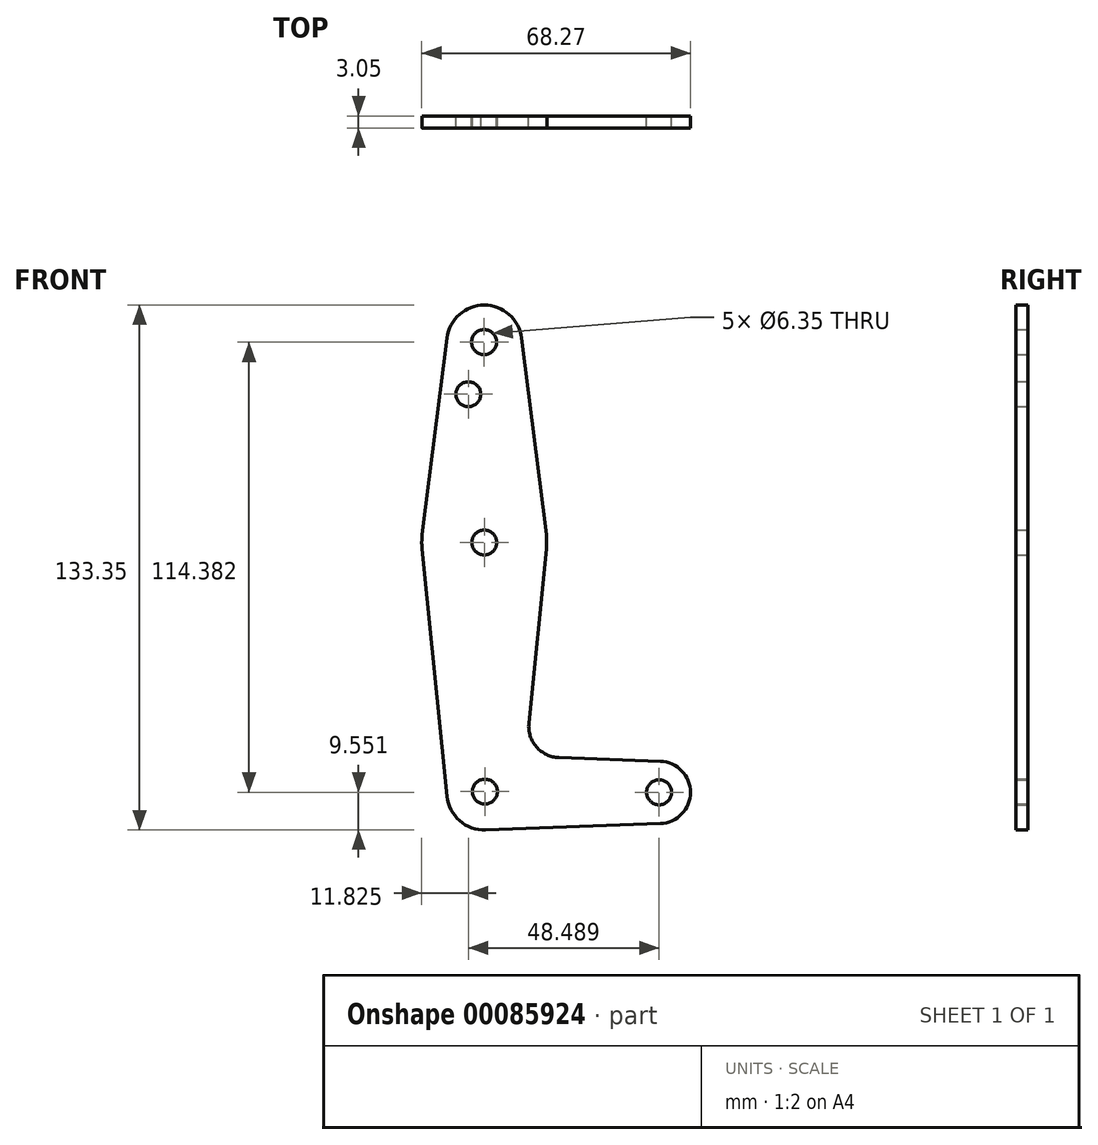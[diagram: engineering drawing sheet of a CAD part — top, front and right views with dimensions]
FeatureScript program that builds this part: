
annotation { "Feature Type Name" : "Feature", "Feature Type Description" : "" }
export const myFeature = defineFeature(function(context is Context, id is Id, definition is map)
    precondition{}
    {
        {
            var Q0;
            Q0=qCreatedBy(makeId("Front.planeOp"),FACE);
            var sketch = newSketch(context, id + "F0", { "sketchPlane" : qUnion([Q0])});
            skLineSegment(sketch, "E0", {"start": v(0, 114.3) * mm, "end": v(0, 0) * mm, "construction": true});
            skLineSegment(sketch, "E1", {"start": v(0, 0) * mm, "end": v(44.45, 0) * mm, "construction": true});
            skCircle(sketch, "E2", {"center": v(0, 0) * mm, "radius": 9.53 * mm});
            skCircle(sketch, "E3", {"center": v(0, 63.5) * mm, "radius": 15.88 * mm});
            skCircle(sketch, "E4", {"center": v(0, 114.3) * mm, "radius": 9.53 * mm});
            skCircle(sketch, "E5", {"center": v(44.45, 0) * mm, "radius": 7.94 * mm});
            skLineSegment(sketch, "E6", {"start": v(-9.45, 115.5) * mm, "end": v(-15.75, 65.48) * mm});
            skCircle(sketch, "E7", {"center": v(-0.05, 114.41) * mm, "radius": 3.18 * mm});
            skCircle(sketch, "E8", {"center": v(0, 63.5) * mm, "radius": 3.18 * mm});
            skCircle(sketch, "E9", {"center": v(0.16, 0.2) * mm, "radius": 3.18 * mm});
            skCircle(sketch, "E10", {"center": v(44.43, 0.03) * mm, "radius": 3.18 * mm});
            skCircle(sketch, "E11", {"center": v(-4.05, 101.17) * mm, "radius": 3.18 * mm});
            skLineSegment(sketch, "E12", {"start": v(15.75, 65.48) * mm, "end": v(9.45, 115.5) * mm});
            skLineSegment(sketch, "E13", {"start": v(15.8, 61.91) * mm, "end": v(11.34, 17.6) * mm});
            skLineSegment(sketch, "E14", {"start": v(0.34, -9.52) * mm, "end": v(44.73, -7.93) * mm});
            skLineSegment(sketch, "E15", {"start": v(18.97, 8.85) * mm, "end": v(44.73, 7.93) * mm});
            skLineSegment(sketch, "E16", {"start": v(-15.8, 61.91) * mm, "end": v(-9.48, -0.95) * mm});
            skArc(sketch, "E17.filletArc", {"start": v(11.34, 17.6) * mm, "mid": v(13.26, 11.57) * mm, "end": v(18.97, 8.85) * mm});
            skText(sketch, "E18", { "text": "The volume of the object is 0.702 in3.", "fontName": "OpenSans-Regular.ttf"});
            const initialGuessF0  = {"E18": [-0.11229, -0.05677, 1, 0, 0.02676]};
            skSetInitialGuess(sketch, initialGuessF0);
            skSolve(sketch);
        }
        {
            var Q0;
            {var subQ0=sQuery(id+"F0.wireOp",EDGE,"E6");Q0=makeQuery(id+"F0.imprint","IMPRINT",FACE,{"disambiguationData":[TD([[makeQuery(id+"F0.imprint","IMPRINT",EDGE,{"derivedFrom":subQ0}),1.0]])]});}
            var Q1;
            Q1=makeQuery(id+"F0.imprint","IMPRINT",FACE,{"disambiguationData":[TD([[makeQuery(id+"F0.imprint","IMPRINT",EDGE,{"derivedFrom":sQuery(id+"F0.wireOp",EDGE,"E7")}),-1.0]])]});
            var Q2;
            Q2=makeQuery(id+"F0.imprint","IMPRINT",FACE,{"disambiguationData":[TD([[makeQuery(id+"F0.imprint","IMPRINT",EDGE,{"derivedFrom":sQuery(id+"F0.wireOp",EDGE,"E8")}),-1.0]])]});
            var Q3;
            {var subQ5=sQuery(id+"F0.wireOp",EDGE,"E13");Q3=makeQuery(id+"F0.imprint","IMPRINT",FACE,{"disambiguationData":[TD([[makeQuery(id+"F0.imprint","IMPRINT",EDGE,{"derivedFrom":subQ5}),-1.0]])]});}
            var Q4;
            Q4=makeQuery(id+"F0.imprint","IMPRINT",FACE,{"disambiguationData":[TD([[makeQuery(id+"F0.imprint","IMPRINT",EDGE,{"derivedFrom":sQuery(id+"F0.wireOp",EDGE,"E9")}),-1.0]])]});
            var Q5;
            Q5=makeQuery(id+"F0.imprint","IMPRINT",FACE,{"disambiguationData":[TD([[makeQuery(id+"F0.imprint","IMPRINT",EDGE,{"derivedFrom":sQuery(id+"F0.wireOp",EDGE,"E10")}),-1.0]])]});
            extrude(context, id + "F1", {"entities" : qUnion([Q0, Q1, Q2, Q3, Q4, Q5]), "depth" : 3.05 * mm});
        }
    });
